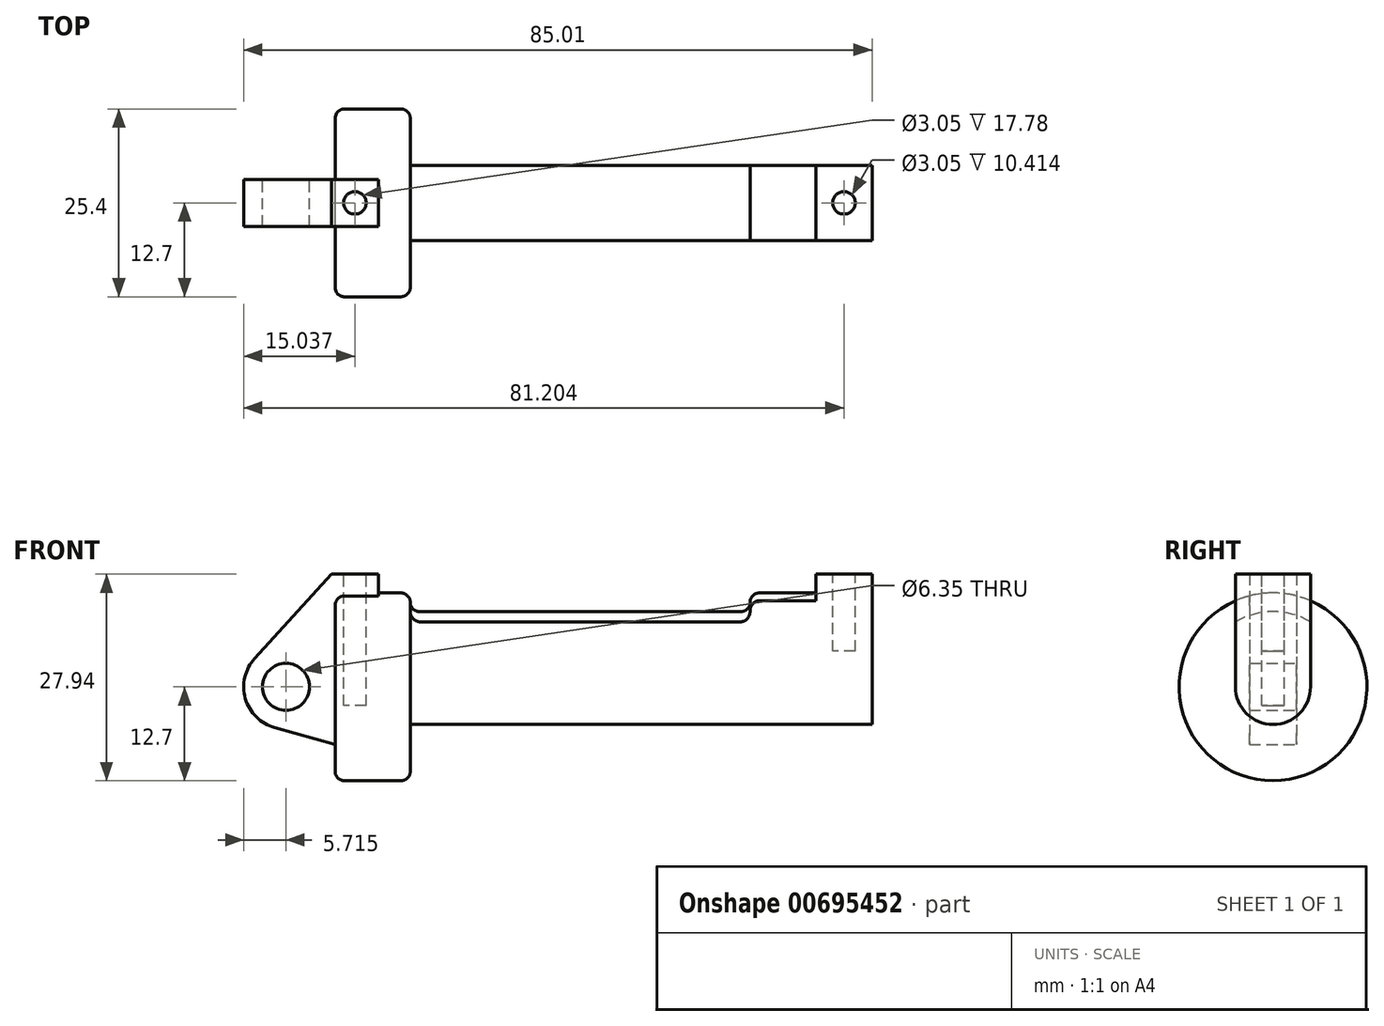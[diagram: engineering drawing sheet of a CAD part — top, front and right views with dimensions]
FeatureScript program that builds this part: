
annotation { "Feature Type Name" : "Feature", "Feature Type Description" : "" }
export const myFeature = defineFeature(function(context is Context, id is Id, definition is map)
    precondition{}
    {
        {
            var Q0;
            Q0=qCreatedBy(makeId("Front.planeOp"),FACE);
            var sketch = newSketch(context, id + "F0", { "sketchPlane" : qUnion([Q0])});
            skLineSegment(sketch, "E0", {"start": v(0, 0) * mm, "end": v(0, 12.7) * mm});
            skLineSegment(sketch, "E1", {"start": v(0, 12.7) * mm, "end": v(10.16, 12.7) * mm});
            skLineSegment(sketch, "E2", {"start": v(10.16, 12.7) * mm, "end": v(10.16, 10.16) * mm});
            skLineSegment(sketch, "E3", {"start": v(10.16, 10.16) * mm, "end": v(56.13, 10.16) * mm});
            skLineSegment(sketch, "E4", {"start": v(56.13, 10.16) * mm, "end": v(56.13, 12.7) * mm});
            skLineSegment(sketch, "E5", {"start": v(56.13, 12.7) * mm, "end": v(66.3, 12.7) * mm});
            skLineSegment(sketch, "E6", {"start": v(66.3, 12.7) * mm, "end": v(66.3, 0) * mm});
            skLineSegment(sketch, "E7", {"start": v(66.3, 0) * mm, "end": v(0, 0) * mm});
            skLineSegment(sketch, "E8", {"start": v(5.84, 15.24) * mm, "end": v(-0.5, 15.24) * mm});
            skLineSegment(sketch, "E9", {"start": v(-0.5, 15.24) * mm, "end": v(-10.88, 3.85) * mm});
            skLineSegment(sketch, "E10", {"start": v(0, 0) * mm, "end": v(-6.65, 0) * mm});
            skCircle(sketch, "E11", {"center": v(-6.65, 0) * mm, "radius": 5.72 * mm});
            skCircle(sketch, "E12", {"center": v(-6.65, 0) * mm, "radius": 3.18 * mm});
            skLineSegment(sketch, "E13", {"start": v(5.84, 15.24) * mm, "end": v(5.84, -9.4) * mm});
            skLineSegment(sketch, "E14", {"start": v(5.84, -9.4) * mm, "end": v(-8.18, -5.5) * mm});
            skSolve(sketch);
        }
        {
            var Q0;
            {var subQ0=sQuery(id+"F0.wireOp",EDGE,"E0");Q0=makeQuery(id+"F0.imprint","IMPRINT",FACE,{"disambiguationData":[TD([[makeQuery(id+"F0.imprint","IMPRINT",EDGE,{"derivedFrom":subQ0}),-1.0]])]});}
            var Q1;
            {var subQ0=sQuery(id+"F0.wireOp",EDGE,"E2");Q1=makeQuery(id+"F0.imprint","IMPRINT",FACE,{"disambiguationData":[TD([[makeQuery(id+"F0.imprint","IMPRINT",EDGE,{"derivedFrom":subQ0}),-1.0]])]});}
            var Q2;
            Q2=sQuery(id+"F0.wireOp",EDGE,"E7");
            revolve(context, id + "F1", {"entities" : qUnion([Q0, Q1]), "axis" : qUnion([Q2]), "revolveType" : RevolveType.FULL});
        }
        {
            var Q0;
            {var subQ1=sQuery(id+"F0.wireOp",EDGE,"E0");Q0=makeQuery(id+"F0.imprint","IMPRINT",FACE,{"disambiguationData":[TD([[makeQuery(id+"F0.imprint","IMPRINT",EDGE,{"derivedFrom":subQ1}),1.0]])]});}
            var Q1;
            {var subQ0=sQuery(id+"F0.wireOp",EDGE,"E0");Q1=makeQuery(id+"F0.imprint","IMPRINT",FACE,{"disambiguationData":[TD([[makeQuery(id+"F0.imprint","IMPRINT",EDGE,{"derivedFrom":subQ0}),-1.0]])]});}
            var Q2;
            {var subQ0=sQuery(id+"F0.wireOp",EDGE,"E14");Q2=makeQuery(id+"F0.imprint","IMPRINT",FACE,{"disambiguationData":[TD([[makeQuery(id+"F0.imprint","IMPRINT",EDGE,{"derivedFrom":subQ0}),-1.0]])]});}
            var Q3;
            {var subQ5=sQuery(id+"F0.wireOp",EDGE,"E12");Q3=makeQuery(id+"F0.imprint","IMPRINT",FACE,{"disambiguationData":[TD([[makeQuery(id+"F0.imprint","IMPRINT",EDGE,{"derivedFrom":subQ5}),-1.0]])]});}
            extrude(context, id + "F2", {"entities" : qUnion([Q0, Q1, Q2, Q3]), "operationType" : NewBodyOperationType.ADD, "depth" : 6.35 * mm, "offsetDistance" : 25.4 * mm, "symmetric" : true});
        }
        {
            var Q0;
            Q0=makeQuery(id+"F1.opRevolve","SWEPT_FACE",FACE,{"disambiguationData":[OSD([sQuery(id+"F0.wireOp",EDGE,"E6")])]});
            var sketch = newSketch(context, id + "F3", { "sketchPlane" : qUnion([Q0])});
            skCircle(sketch, "E15", {"center": v(0, 0) * mm, "radius": 1.52 * mm});
            skCircle(sketch, "E16", {"center": v(0, 0) * mm, "radius": 5.08 * mm});
            skLineSegment(sketch, "E17", {"start": v(-5.08, 0) * mm, "end": v(-5.08, 15.24) * mm});
            skLineSegment(sketch, "E18", {"start": v(-5.08, 15.24) * mm, "end": v(5.08, 15.24) * mm});
            skLineSegment(sketch, "E19", {"start": v(5.08, 15.24) * mm, "end": v(5.08, 0) * mm});
            skSolve(sketch);
        }
        {
            var Q0;
            Q0=makeQuery(id+"F3.imprint","IMPRINT",FACE,{"disambiguationData":[TD([[makeQuery(id+"F3.imprint","IMPRINT",EDGE,{"derivedFrom":sQuery(id+"F3.wireOp",EDGE,"E15")}),-1.0]])]});
            var Q1;
            {var subQ0=sQuery(id+"F3.wireOp",EDGE,"E18");Q1=makeQuery(id+"F3.imprint","IMPRINT",FACE,{"disambiguationData":[TD([[makeQuery(id+"F3.imprint","IMPRINT",EDGE,{"derivedFrom":subQ0}),-1.0]])]});}
            var Q2;
            {var subQ0=sQuery(id+"F3.wireOp",EDGE,"E17");var subQ1=sQuery(id+"F3.wireOp",EDGE,"E16");var subQ2=makeQuery(id+"F3.imprint","INTERSECT",VERTEX,{"derivedFrom":[subQ1,subQ0]});Q2=makeQuery(id+"F3.imprint","IMPRINT",FACE,{"disambiguationData":[TD([[makeQuery(id+"F3.imprint","IMPRINT",EDGE,{"disambiguationData":[TD([[subQ2,1.0]])],"derivedFrom":subQ1}),-1.0]])]});}
            extrude(context, id + "F4", {"entities" : qUnion([Q0, Q1, Q2]), "operationType" : NewBodyOperationType.ADD, "depth" : 6.35 * mm, "offsetDistance" : 25.4 * mm, "hasSecondDirection" : true, "secondDirectionOppositeDirection" : true, "secondDirectionDepth" : 1.27 * mm});
        }
        {
            var Q0;
            Q0=makeQuery(id+"F4.boolean.opBoolean","SPLIT",FACE,{"disambiguationData":[TD([makeQuery(id+"F4.opExtrude","SWEPT_FACE",FACE,{"disambiguationData":[OSD([sQuery(id+"F3.wireOp",EDGE,"E15")])]})])],"derivedFrom":makeQuery(id+"F1.opRevolve","SWEPT_FACE",FACE,{"disambiguationData":[OSD([sQuery(id+"F0.wireOp",EDGE,"E6")])]})});
            var Q1;
            Q1=makeQuery(id+"F1.opRevolve","SWEPT_FACE",FACE,{"disambiguationData":[OSD([sQuery(id+"F0.wireOp",EDGE,"E2")])]});
            extrude(context, id + "F5", {"entities" : qUnion([Q0]), "operationType" : NewBodyOperationType.REMOVE, "endBound" : BoundingType.UP_TO_SURFACE, "oppositeDirection" : true, "depth" : 25.4 * mm, "endBoundEntityFace" : qUnion([Q1]), "offsetDistance" : 25.4 * mm});
        }
        {
            var Q0;
            Q0=makeQuery(id+"F2.opExtrude","SWEPT_FACE",FACE,{"disambiguationData":[OSD([sQuery(id+"F0.wireOp",EDGE,"E8")])]});
            var sketch = newSketch(context, id + "F6", { "sketchPlane" : qUnion([Q0])});
            skCircle(sketch, "E20", {"center": v(68.83, 0) * mm, "radius": 1.52 * mm});
            skPoint(sketch, "E20.centerSnap0", {"position": v(68.83, 5.08) * mm});
            skPoint(sketch, "E20.centerSnap1", {"position": v(65.02, 0) * mm});
            skCircle(sketch, "E21", {"center": v(2.67, 0) * mm, "radius": 1.52 * mm});
            skPoint(sketch, "E21.centerSnap0", {"position": v(-0.5, 0) * mm});
            skPoint(sketch, "E21.centerSnap1", {"position": v(2.67, 3.18) * mm});
            skSolve(sketch);
        }
        {
            var Q0;
            Q0=makeQuery(id+"F6.imprint","IMPRINT",FACE,{"disambiguationData":[TD([[makeQuery(id+"F6.imprint","IMPRINT",EDGE,{"derivedFrom":sQuery(id+"F6.wireOp",EDGE,"E21")}),1.0]])]});
            extrude(context, id + "F7", {"entities" : qUnion([Q0]), "operationType" : NewBodyOperationType.REMOVE, "oppositeDirection" : true, "depth" : 17.78 * mm, "offsetDistance" : 25.4 * mm});
        }
        {
            var Q0;
            Q0=makeQuery(id+"F6.imprint","IMPRINT",FACE,{"disambiguationData":[TD([[makeQuery(id+"F6.imprint","IMPRINT",EDGE,{"derivedFrom":sQuery(id+"F6.wireOp",EDGE,"E20")}),1.0]])]});
            extrude(context, id + "F8", {"entities" : qUnion([Q0]), "operationType" : NewBodyOperationType.REMOVE, "oppositeDirection" : true, "depth" : 10.4 * mm, "offsetDistance" : 25.4 * mm});
        }
        {
            var Q0;
            Q0=makeQuery(id+"F1.opRevolve","SWEPT_EDGE",EDGE,{"disambiguationData":[OSD([sQuery(id+"F0.wireOp",EDGE,"E1"),sQuery(id+"F0.wireOp",EDGE,"E2")])]});
            var Q1;
            Q1=makeQuery(id+"F1.opRevolve","SWEPT_EDGE",EDGE,{"disambiguationData":[OSD([sQuery(id+"F0.wireOp",EDGE,"E4"),sQuery(id+"F0.wireOp",EDGE,"E5")])]});
            var Q2;
            Q2=makeQuery(id+"F1.opRevolve","SWEPT_EDGE",EDGE,{"disambiguationData":[OSD([sQuery(id+"F0.wireOp",EDGE,"E2"),sQuery(id+"F0.wireOp",EDGE,"E3")])]});
            var Q3;
            Q3=makeQuery(id+"F1.opRevolve","SWEPT_EDGE",EDGE,{"disambiguationData":[OSD([sQuery(id+"F0.wireOp",EDGE,"E3"),sQuery(id+"F0.wireOp",EDGE,"E4")])]});
            var Q4;
            Q4=makeQuery(id+"F1.opRevolve","SWEPT_EDGE",EDGE,{"disambiguationData":[OSD([sQuery(id+"F0.wireOp",EDGE,"E5"),sQuery(id+"F0.wireOp",EDGE,"E6")])]});
            var Q5;
            Q5=makeQuery(id+"F1.opRevolve","SWEPT_EDGE",EDGE,{"disambiguationData":[OSD([sQuery(id+"F0.wireOp",EDGE,"E0"),sQuery(id+"F0.wireOp",EDGE,"E1")])]});
            fillet(context, id + "F9", {"entities" : qUnion([Q0, Q1, Q2, Q3, Q4, Q5]), "radius" : 1.27 * mm, "tangentPropagation" : true, "allowEdgeOverflow" : false});
        }
    });
